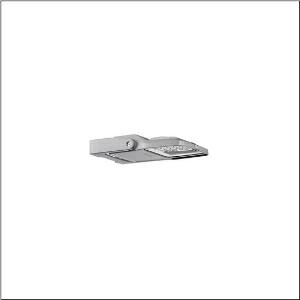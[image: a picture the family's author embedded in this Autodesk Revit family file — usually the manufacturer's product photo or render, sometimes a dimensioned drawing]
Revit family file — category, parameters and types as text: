
# Revit family: floodlight_fl_21_iq_micro___pl43_5xa7761a4a2a_9599
name_source: partatom
category: Lighting Fixtures
units: mm (PartAtom-declared; Revit-internal decimal feet)

## family parameters
Cut with Voids When Loaded = No
Host = Face
Light Source = No
Part Type = Normal
Room Calculation Point = No
Round Connector Dimension = Use Diameter
Shared = No

## types (1)
- --- (1 x LED, 3170 lm, 23.1 W, 4000K)
    Apparent Load = 23 VA
    CIE Flux Codes = 29 80 99 100 100
    Color Rendering = 70
    Color Temperature = 4000K
    Default Elevation = 1800 mm
    Description = Floodlight FL 21 iQ micro, floodlight, primary light control with lens, of PMMA, primary optical cover: protective disc, of toughened safety glass, transparent, light distribution: PL43, light emission: direct distribution, installation type: surface-mounted, LED, High Power LED, rated luminous flux: 3.170lm, luminous efficacy: 137lm/W, light colour: 740, colour temperature: 4000K, control: optimised constant luminous flux control (CLO 2.0), Desk-Remote (wireless, voltage-free reading and setting of iQ features in the workshop via application-optimized NFC function/RFID function), Light-Fading, Smart-Wire, Night-Set, Lumen-Switch, Temp-Guard, Auto-Match, with terminal, 6-pole, mains connection: 220..240V, AC, 50/60Hz, start of lifetime: 23W, end of service life: 24W, reduction: 11W, luminaire housing, of diecast aluminium, powder-coated, Siteco® metallic grey (DB 702S), corrosivity category C5 mid according to DIN EN ISO 12944, sealing non-destructively replaceable, design bracket, of diecast aluminium, powder-coated, Siteco® metallic grey (DB 702S), protection rating (complete): IP66, insulation class (complete): insulation class II (safety insulation), certification: CE, ENEC, VDE, protection symbol: D, impact resistance: IK07, permissible operating ambient temperature: -40..+40°C, permissible operating ambient temperature for outdoor applications: -40..+50°C, standard: DIN EN 12944, LABS conformity tested according to VDMA 24364:2018-05, packaging unit: 1 piece

Light Distribution: PL43
    Height = 65 mm
    Lamp = 1 x LED
    Lamp Light Flux = 3170 lm
    Lamp Power = 23.1 W
    Lamp count = 1
    Length = 312 mm
    Luminous efficacy = 137 lm/W
    Manufacturer = Siteco
    ModVariant = No
    Model = 5XA7761A4A2A
    Mounting Place = Wall
    Mounting Type = Surface mounted
    Number of Poles = 1
    OnlyDefault = Yes
    Power Factor = 1
    Product Name = Floodlight FL 21 iQ micro | PL43
    Product group = floodlight | wall mounted
    ProductGroupID = 2001
    Protection Class = Protection class II
    Protection Degree = IP 66
    RLX_Detail_Level = 1
    RLX_Emergency_Light_Flux = 0 lm
    RLX_Emergency_Type = 0
    RLX_Emergency_Type_DB = No
    RlxData = <blob elided: 97321 chars, md5=002cef7b>
    Socket = socket
    Standby Power = 0 W
    System Light Flux = 3170 lm
    System Power = 23 W
    Type Comments = factory setting: luminous flux: 100 % | dim-lin: 254 | 455 mA
    Type Image = l_1006878.jpg
    URL = http://relux.com
    VarID = @adj_127919
    Voltage = 0 V
    Weight = 0.00 kg
    Width = 230 mm

## geometry (parser evidence)
native form markers: Blend x4, Sweep x12
no freeform markers — native parametric forms only
